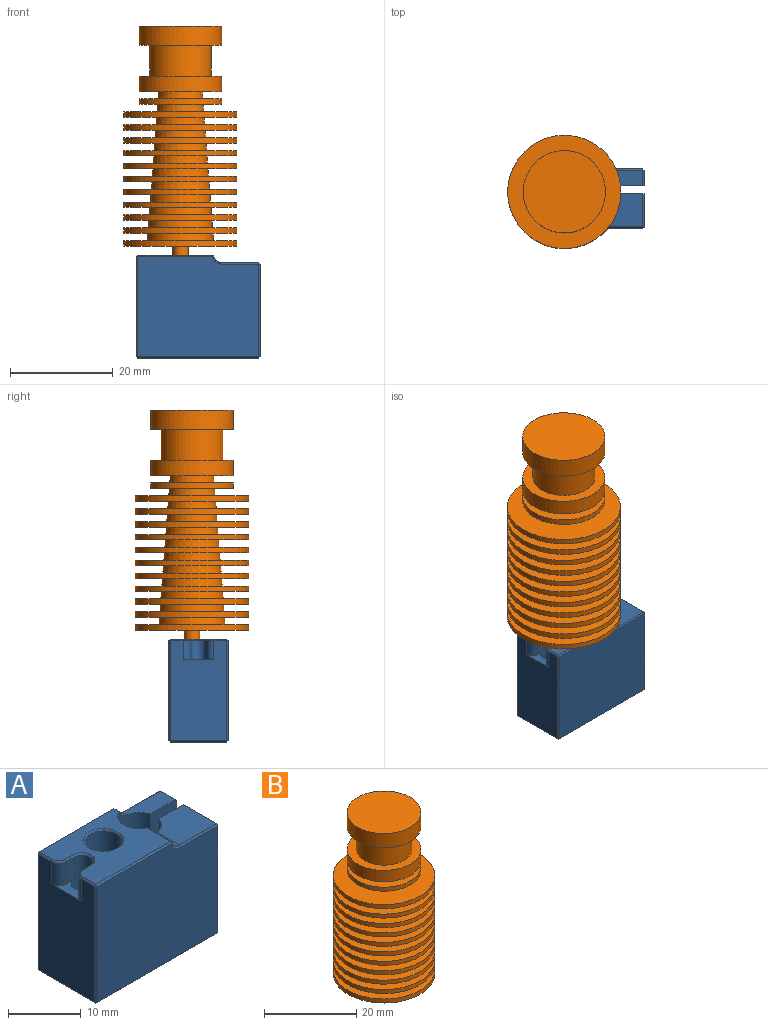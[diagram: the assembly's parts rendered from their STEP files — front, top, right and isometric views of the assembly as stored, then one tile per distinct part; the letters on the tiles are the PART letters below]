
ASSEMBLY  parts=2 mates=1
PART A: 61 faces, bbox 24x11.5x20 mm
  f0: plane 14.52x11mm, normal (0,0,1), area 113.9mm2, adj f11,f21,f27,f33,f39,f43,f47,f48
  f1: plane 19.5x11mm, normal (-1,0,0), area 192mm2, adj f18,f19,f20,f33,f34,f44,f52,f56
  f2: plane 18x2.95mm, normal (1,0,0), area 53.1mm2, adj f12,f32,f36,f37
  f3: plane 7.25x2.95mm, normal (0,0,1), area 17.8mm2, adj f8,f11,f12,f32,f42
  f4: cylinder r=1.5mm len=4.42mm, axis (0,1,0), area 9.2mm2, adj f7,f11,f21,f22
  f5: plane 23.5x11mm, normal (0,0,-1), area 184.7mm2, adj f12,f13,f29,f35,f36,f44,f45,f58
  f6: plane 18x6.45mm, normal (1,0,0), area 116.1mm2, adj f13,f24,f28,f29
  f7: plane 7.25x6.45mm, normal (0,0,1), area 43.2mm2, adj f4,f11,f13,f23,f24
  f8: cylinder r=1.5mm len=1.48mm, axis (0,1,0), area 1.7mm2, adj f3,f11,f46,f47
  f9: plane 23.5x19.5mm, normal (0,-1,0), area 445.4mm2, adj f22,f23,f27,f28,f34,f35
  f10: plane 23.5x19.5mm, normal (0,1,0), area 445.4mm2, adj f37,f42,f45,f46,f52,f53
  f11: cylinder r=3mm len=19.75mm, axis (0,0,-1), area 326.5mm2, adj f0,f3,f4,f7,f8,f12,f13,f21
  f12: plane 18.5x5.11mm, normal (0,-1,0), area 94.4mm2, adj f2,f3,f5,f11,f32,f36,f60
  f13: plane 18.5x5.11mm, normal (0,1,0), area 94.4mm2, adj f5,f6,f7,f11,f24,f29,f60
  f14: cylinder r=2.5mm len=19.5mm, axis (0,0,-1), area 306.3mm2, adj f57,f59
  f15: cylinder r=1.5mm len=19.5mm, axis (0,0,-1), area 166.1mm2, adj f16,f17,f18,f48,f58
  f16: plane 3.75x1.5mm, normal (0,-1,0), area 5.6mm2, adj f15,f18,f19,f51
  f17: plane 3.75x1.5mm, normal (0,1,0), area 5.6mm2, adj f15,f18,f20,f43
  f18: plane 6x3mm, normal (0,0,1), area 6.4mm2, adj f1,f15,f16,f17,f19,f20
  f19: cylinder r=1.5mm len=3.75mm, axis (0,0,1), area 8.8mm2, adj f1,f16,f18,f54
  f20: cylinder r=1.5mm len=3.75mm, axis (0,0,-1), area 8.8mm2, adj f1,f17,f18,f39
  f21: plane 4.52x0.25mm, normal (0.65,0,0.76), area 1.5mm2, adj f0,f4,f11,f25
  f22: cone r=1.5mm half-angle=45deg, axis (0,-1,0), area 0.8mm2, adj f4,f9,f23,f25
  f23: plane 7.25x0.25mm, normal (0,-0.71,0.71), area 2.6mm2, adj f7,f9,f22,f26
  f24: plane 6.45x0.25mm, normal (0.71,0,0.71), area 2.3mm2, adj f6,f7,f13,f26
  f25: plane 0.25x0.25mm, normal (0.52,-0.6,0.6), area 0.1mm2, adj f21,f22,f27
  f26: plane 0.25x0.25mm, normal (0.58,-0.58,0.58), area 0.1mm2, adj f23,f24,f28
  f27: plane 14.52x0.25mm, normal (0,-0.71,0.71), area 5.1mm2, adj f0,f9,f25,f30
  f28: plane 18x0.25mm, normal (0.71,-0.71,0), area 6.4mm2, adj f6,f9,f26,f31
  f29: plane 6.45x0.25mm, normal (0.71,0,-0.71), area 2.3mm2, adj f5,f6,f13,f31
  f30: plane 0.25x0.25mm, normal (-0.58,-0.58,0.58), area 0.1mm2, adj f27,f33,f34
  f31: plane 0.25x0.25mm, normal (0.58,-0.58,-0.58), area 0.1mm2, adj f28,f29,f35
  f32: plane 2.95x0.25mm, normal (0.71,0,0.71), area 1mm2, adj f2,f3,f12,f38
  f33: plane 2.48x0.25mm, normal (-0.71,0,0.71), area 0.9mm2, adj f0,f1,f30,f39
  f34: plane 19.5x0.25mm, normal (-0.71,-0.71,0), area 6.9mm2, adj f1,f9,f30,f40
  f35: plane 23.5x0.25mm, normal (0,-0.71,-0.71), area 8.3mm2, adj f5,f9,f31,f40
  f36: plane 2.95x0.25mm, normal (0.71,0,-0.71), area 1mm2, adj f2,f5,f12,f41
  f37: plane 18x0.25mm, normal (0.71,0.71,0), area 6.4mm2, adj f2,f10,f38,f41
  f38: plane 0.25x0.25mm, normal (0.58,0.58,0.58), area 0.1mm2, adj f32,f37,f42
  f39: cone r=1.25mm half-angle=45deg, axis (0,0,-1), area 0.8mm2, adj f0,f20,f33,f43
  f40: plane 0.25x0.25mm, normal (-0.58,-0.58,-0.58), area 0.1mm2, adj f34,f35,f44
  f41: plane 0.25x0.25mm, normal (0.58,0.58,-0.58), area 0.1mm2, adj f36,f37,f45
  f42: plane 7.25x0.25mm, normal (0,0.71,0.71), area 2.6mm2, adj f3,f10,f38,f46
  f43: plane 1.5x0.25mm, normal (0,0.71,0.71), area 0.5mm2, adj f0,f17,f39,f48
  f44: plane 11x0.25mm, normal (-0.71,0,-0.71), area 3.9mm2, adj f1,f5,f40,f49
  f45: plane 23.5x0.25mm, normal (0,0.71,-0.71), area 8.3mm2, adj f5,f10,f41,f49
  f46: cone r=1.75mm half-angle=45deg, axis (0,1,0), area 0.8mm2, adj f8,f10,f42,f50
  f47: plane 1.02x0.25mm, normal (0.65,0,0.76), area 0.3mm2, adj f0,f8,f11,f50
  f48: cone r=1.75mm half-angle=45deg, axis (0,0,1), area 1.8mm2, adj f0,f15,f43,f51
  f49: plane 0.25x0.25mm, normal (-0.58,0.58,-0.58), area 0.1mm2, adj f44,f45,f52
  f50: plane 0.25x0.25mm, normal (0.52,0.6,0.6), area 0.1mm2, adj f46,f47,f53
  f51: plane 1.5x0.25mm, normal (0,-0.71,0.71), area 0.5mm2, adj f0,f16,f48,f54
  f52: plane 19.5x0.25mm, normal (-0.71,0.71,0), area 6.9mm2, adj f1,f10,f49,f55
  f53: plane 14.52x0.25mm, normal (0,0.71,0.71), area 5.1mm2, adj f0,f10,f50,f55
  f54: cone r=1.25mm half-angle=45deg, axis (0,0,-1), area 0.8mm2, adj f0,f19,f51,f56
  f55: plane 0.25x0.25mm, normal (-0.58,0.58,0.58), area 0.1mm2, adj f52,f53,f56
  f56: plane 2.52x0.25mm, normal (-0.71,0,0.71), area 0.9mm2, adj f0,f1,f54,f55
  f57: cone r=2.75mm half-angle=45deg, axis (0,0,1), area 5.8mm2, adj f0,f14
  f58: cone r=1.5mm half-angle=45deg, axis (0,0,-1), area 3.6mm2, adj f5,f15
  f59: cone r=2.5mm half-angle=45deg, axis (0,0,-1), area 5.8mm2, adj f5,f14
  f60: cone r=3mm half-angle=45deg, axis (0,0,-1), area 6.4mm2, adj f5,f11,f12,f13
PART B: 57 faces, bbox 22x22x44.8 mm
  f0: cylinder r=11mm len=22mm, axis (0,0,1), area 72.6mm2, adj f1,f56
  f1: plane 22x22mm, normal (0,0,-1), area 312.9mm2, adj f0,f2
  f2: cone r=4.62mm half-angle=4.3deg, axis (0,0,-1), area 42.8mm2, adj f1,f3
  f3: plane 22x22mm, normal (0,0,1), area 309.7mm2, adj f2,f4
  f4: cylinder r=11mm len=22mm, axis (0,0,1), area 72.6mm2, adj f3,f5
  f5: plane 22x22mm, normal (0,0,-1), area 307.4mm2, adj f4,f6
  f6: cone r=4.81mm half-angle=4.3deg, axis (0,0,-1), area 44.5mm2, adj f5,f7
  f7: plane 22x22mm, normal (0,0,1), area 304mm2, adj f6,f8
  f8: cylinder r=11mm len=22mm, axis (0,0,1), area 72.6mm2, adj f7,f9
  f9: plane 22x22mm, normal (0,0,-1), area 301.6mm2, adj f8,f10
  f10: cone r=5mm half-angle=4.3deg, axis (0,0,-1), area 46.2mm2, adj f9,f11
  f11: plane 22x22mm, normal (0,0,1), area 298.1mm2, adj f10,f12
  f12: cylinder r=11mm len=22mm, axis (0,0,1), area 72.6mm2, adj f11,f13
  f13: plane 22x22mm, normal (0,0,-1), area 295.6mm2, adj f12,f14
  f14: cone r=5.19mm half-angle=4.3deg, axis (0,0,-1), area 47.9mm2, adj f13,f15
  f15: plane 22x22mm, normal (0,0,1), area 292mm2, adj f14,f16
  f16: cylinder r=11mm len=22mm, axis (0,0,1), area 72.6mm2, adj f15,f17
  f17: plane 22x22mm, normal (0,0,-1), area 289.4mm2, adj f16,f18
  f18: cone r=5.38mm half-angle=4.3deg, axis (0,0,-1), area 49.6mm2, adj f17,f19
  f19: plane 22x22mm, normal (0,0,1), area 285.7mm2, adj f18,f20
  f20: cylinder r=11mm len=22mm, axis (0,0,1), area 72.6mm2, adj f19,f21
  f21: plane 22x22mm, normal (0,0,-1), area 282.9mm2, adj f20,f22
  f22: cone r=5.56mm half-angle=4.3deg, axis (0,0,-1), area 51.3mm2, adj f21,f23
  f23: plane 22x22mm, normal (0,0,1), area 279.1mm2, adj f22,f24
  f24: cylinder r=11mm len=22mm, axis (0,0,1), area 72.6mm2, adj f23,f25
  f25: plane 22x22mm, normal (0,0,-1), area 276.3mm2, adj f24,f26
  f26: cone r=5.75mm half-angle=4.3deg, axis (0,0,-1), area 53mm2, adj f25,f27
  f27: plane 22x22mm, normal (0,0,1), area 272.3mm2, adj f26,f28
  f28: cylinder r=11mm len=22mm, axis (0,0,1), area 72.6mm2, adj f27,f29
  f29: plane 22x22mm, normal (0,0,-1), area 269.4mm2, adj f28,f30
  f30: cone r=5.94mm half-angle=4.3deg, axis (0,0,-1), area 54.7mm2, adj f29,f31
  f31: plane 22x22mm, normal (0,0,1), area 265.3mm2, adj f30,f32
  f32: cylinder r=11mm len=22mm, axis (0,0,1), area 72.6mm2, adj f31,f33
  f33: plane 22x22mm, normal (0,0,-1), area 262.3mm2, adj f32,f34
  f34: cone r=6.12mm half-angle=4.3deg, axis (0,0,-1), area 56.5mm2, adj f33,f35
  f35: plane 22x22mm, normal (0,0,1), area 258.1mm2, adj f34,f36
  f36: cylinder r=11mm len=22mm, axis (0,0,1), area 72.6mm2, adj f35,f37
  f37: plane 22x22mm, normal (0,0,-1), area 254.9mm2, adj f36,f38
  f38: cone r=6.31mm half-angle=4.3deg, axis (0,0,-1), area 58.2mm2, adj f37,f39
  f39: plane 22x22mm, normal (0,0,1), area 250.6mm2, adj f38,f40
  f40: cylinder r=11mm len=22mm, axis (0,0,1), area 72.6mm2, adj f39,f41
  f41: plane 22x22mm, normal (0,0,-1), area 373.1mm2, adj f40,f42
  f42: cylinder r=1.5mm len=3mm, axis (0,0,1), area 18.8mm2, adj f41,f43
  f43: plane 3x3mm, normal (0,0,-1), area 7.1mm2, adj f42
  f44: plane 16x16mm, normal (0,0,1), area 201.1mm2, adj f45
  f45: cylinder r=8mm len=16mm, axis (0,0,1), area 188.5mm2, adj f44,f46
  f46: plane 16x16mm, normal (0,0,-1), area 88mm2, adj f45,f47
  f47: cylinder r=6mm len=12mm, axis (0,0,1), area 226.2mm2, adj f46,f48
  f48: plane 16x16mm, normal (0,0,1), area 88mm2, adj f47,f49
  f49: cylinder r=8mm len=16mm, axis (0,0,1), area 150.8mm2, adj f48,f50
  f50: plane 16x16mm, normal (0,0,-1), area 144.3mm2, adj f49,f51
  f51: cone r=4.25mm half-angle=4.3deg, axis (0,0,-1), area 38.8mm2, adj f50,f52
  f52: plane 16x16mm, normal (0,0,1), area 141.4mm2, adj f51,f53
  f53: cylinder r=8mm len=16mm, axis (0,0,1), area 53.8mm2, adj f52,f54
  f54: plane 16x16mm, normal (0,0,-1), area 139.2mm2, adj f53,f55
  f55: cone r=4.44mm half-angle=4.3deg, axis (0,0,-1), area 41mm2, adj f54,f56
  f56: plane 22x22mm, normal (0,0,1), area 315.2mm2, adj f0,f55
PLACE A t=(3.5,-10.1,-40)mm
PLACE B t=(0,-14.6,-15.2)mm
MATE cylindrical B.f0 <-> A.f14  axis (0,0,-1) through (0,-14.6,-30.25)mm
